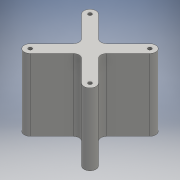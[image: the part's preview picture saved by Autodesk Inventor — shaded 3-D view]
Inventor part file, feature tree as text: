
AUTODESK INVENTOR PART (.ipt)
format: ipt  version: 2016 (Build 200138000, 138)  size: 135,680 bytes
history: native  units: mm
features: extrude x1, sketch x1
ambient origin geometry x8: Origin, YZ Plane, XZ Plane, XY Plane, X Axis, Y Axis, Z Axis, Center Point
bodies: Body1 (feature_tree)
feature tree (2):
  extrude  "Main Body"  Depth=60.0mm
  sketch  "Sketch1"  dims[d0=60.0mm d1=60.0mm d2=5.0mm d3=5.0mm d4=5.0mm d5=5.0mm d7=5.0mm d9=5.0mm d10=3.0mm d11=3.0mm d12=3.0mm d13=3.0mm d17=5.0mm d18=45.0deg d19=70.710678mm d20=55.0mm d21=45.0mm d22=28.284271mm d23=55.0mm d24=42.426407mm d25=28.284271mm d26=5.0mm d27=42.426407mm d28=5.0mm d29=77.781746mm d30=60.0mm d31=0.0mm]
